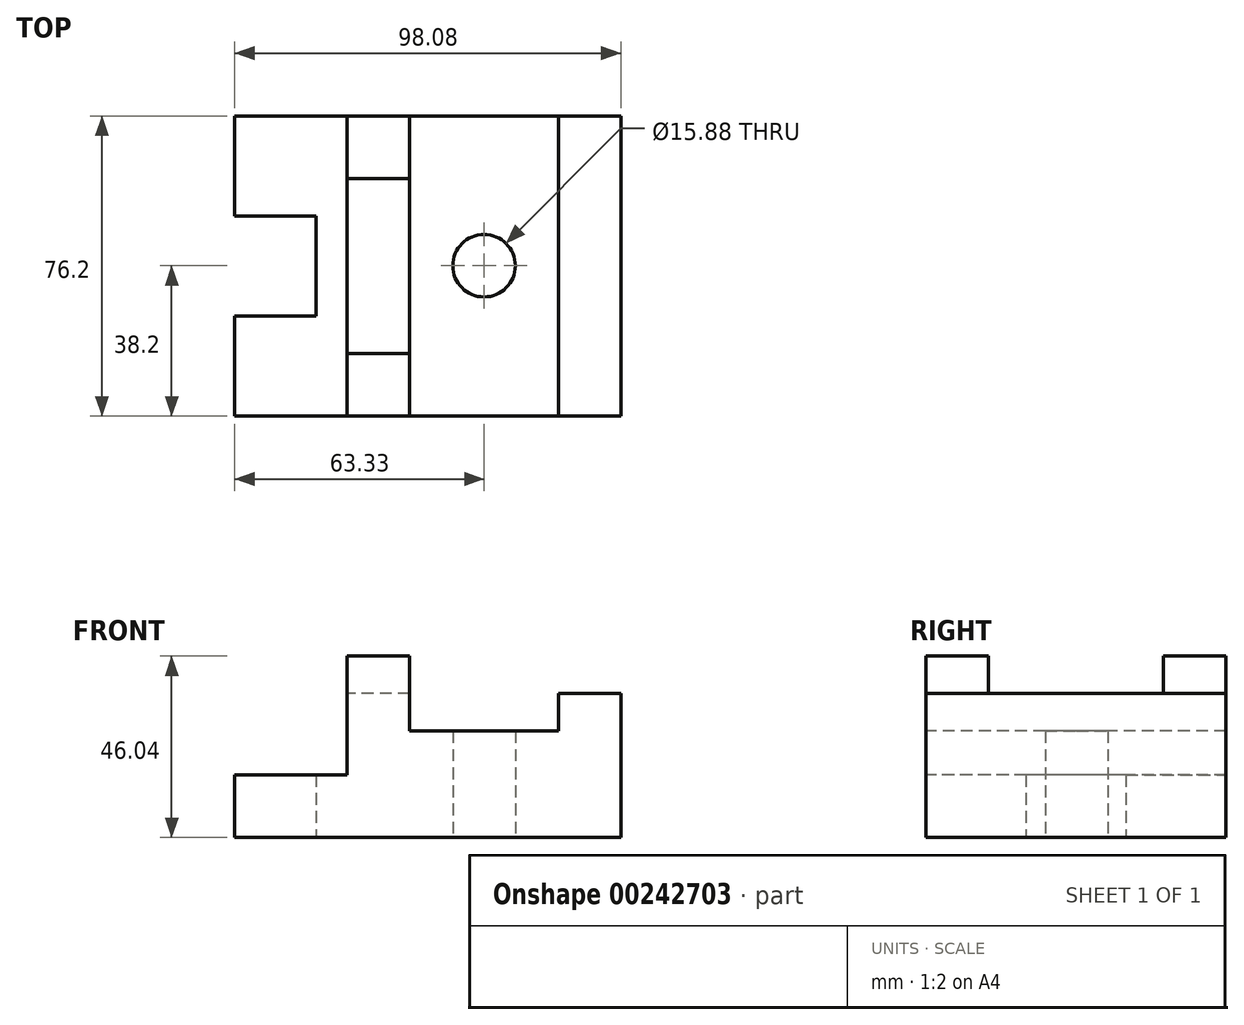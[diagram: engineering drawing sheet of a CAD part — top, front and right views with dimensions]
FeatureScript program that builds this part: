
annotation { "Feature Type Name" : "Feature", "Feature Type Description" : "" }
export const myFeature = defineFeature(function(context is Context, id is Id, definition is map)
    precondition{}
    {
        {
            var Q0;
            Q0=qCreatedBy(makeId("Top.planeOp"),FACE);
            var sketch = newSketch(context, id + "F0", { "sketchPlane" : qUnion([Q0])});
            skLineSegment(sketch, "E0.bottom", {"start": v(-127.34, 76) * mm, "end": v(126.66, 76) * mm});
            skLineSegment(sketch, "E0.top", {"start": v(-127.34, -76.4) * mm, "end": v(126.66, -76.4) * mm});
            skLineSegment(sketch, "E0.right", {"start": v(126.66, 76) * mm, "end": v(126.66, 25.2) * mm});
            skLineSegment(sketch, "E1", {"start": v(126.66, -76.4) * mm, "end": v(126.66, -25.6) * mm});
            skLineSegment(sketch, "E2", {"start": v(126.66, 25.2) * mm, "end": v(126.66, 76) * mm});
            skLineSegment(sketch, "E3", {"start": v(126.66, 25.2) * mm, "end": v(85.38, 25.2) * mm});
            skLineSegment(sketch, "E4", {"start": v(126.66, -25.6) * mm, "end": v(85.38, -25.6) * mm});
            skLineSegment(sketch, "E5", {"start": v(85.38, 25.2) * mm, "end": v(85.38, -25.6) * mm});
            skLineSegment(sketch, "E6", {"start": v(126.66, -76.4) * mm, "end": v(69.5, -76.4) * mm});
            skLineSegment(sketch, "E7", {"start": v(126.66, 76) * mm, "end": v(69.5, 76) * mm});
            skLineSegment(sketch, "E8", {"start": v(69.5, 76) * mm, "end": v(69.5, -76.4) * mm});
            skLineSegment(sketch, "E9", {"start": v(69.5, -76.4) * mm, "end": v(37.76, -76.4) * mm});
            skLineSegment(sketch, "E10", {"start": v(69.5, 76) * mm, "end": v(37.76, 76) * mm});
            skLineSegment(sketch, "E11", {"start": v(37.76, 76) * mm, "end": v(37.76, -76.4) * mm});
            skLineSegment(sketch, "E12", {"start": v(0, 76) * mm, "end": v(0, -76.4) * mm});
            skPoint(sketch, "E12.startSnap0", {"position": v(-0.34, 76) * mm});
            skLineSegment(sketch, "E13", {"start": v(37.76, 76) * mm, "end": v(37.76, 44.25) * mm});
            skLineSegment(sketch, "E14", {"start": v(37.76, 44.25) * mm, "end": v(69.5, 44.25) * mm});
            skLineSegment(sketch, "E15", {"start": v(69.5, 44.25) * mm, "end": v(69.5, 76) * mm});
            skLineSegment(sketch, "E16", {"start": v(37.76, -76.4) * mm, "end": v(37.76, -44.65) * mm});
            skLineSegment(sketch, "E17", {"start": v(37.76, -44.65) * mm, "end": v(69.5, -44.65) * mm});
            skLineSegment(sketch, "E18", {"start": v(69.5, -44.65) * mm, "end": v(69.5, -76.4) * mm});
            skCircle(sketch, "E19", {"center": v(0, 0) * mm, "radius": 15.88 * mm});
            skLineSegment(sketch, "E20.trimOffspring", {"start": v(126.66, -25.6) * mm, "end": v(126.66, -76.4) * mm});
            skLineSegment(sketch, "E21.MirrorCS", {"start": v(-37.76, 76) * mm, "end": v(-37.76, 44.25) * mm});
            skLineSegment(sketch, "E22.MirrorCS", {"start": v(-37.76, 76) * mm, "end": v(-37.76, -76.4) * mm});
            skLineSegment(sketch, "E23.MirrorCS", {"start": v(-37.76, -44.65) * mm, "end": v(-69.5, -44.65) * mm});
            skLineSegment(sketch, "E24.MirrorCS", {"start": v(-69.5, 76) * mm, "end": v(-69.5, -76.4) * mm});
            skLineSegment(sketch, "E25.MirrorCS", {"start": v(-69.5, -76.4) * mm, "end": v(-37.76, -76.4) * mm});
            skLineSegment(sketch, "E26.MirrorCS", {"start": v(-126.66, -25.6) * mm, "end": v(-85.38, -25.6) * mm});
            skLineSegment(sketch, "E27.MirrorCS", {"start": v(-126.66, -25.6) * mm, "end": v(-126.66, -76.4) * mm});
            skLineSegment(sketch, "E28.MirrorCS", {"start": v(-85.38, 25.2) * mm, "end": v(-85.38, -25.6) * mm});
            skLineSegment(sketch, "E29.MirrorCS", {"start": v(-126.66, 25.2) * mm, "end": v(-85.38, 25.2) * mm});
            skLineSegment(sketch, "E30.MirrorCS", {"start": v(-126.66, 25.2) * mm, "end": v(-126.66, 76) * mm});
            skLineSegment(sketch, "E31.MirrorCS", {"start": v(-126.66, 76) * mm, "end": v(-69.5, 76) * mm});
            skLineSegment(sketch, "E32.MirrorCS", {"start": v(-37.76, 44.25) * mm, "end": v(-69.5, 44.25) * mm});
            skPoint(sketch, "E33.MirrorCS.end.orphan", {"position": v(-69.5, -76.4) * mm});
            skPoint(sketch, "E33.MirrorCS.start.orphan", {"position": v(-126.66, -76.4) * mm});
            skLineSegment(sketch, "E34", {"start": v(-126.66, 76) * mm, "end": v(-126.66, 25.2) * mm});
            skSolve(sketch);
        }
        {
            var Q0;
            Q0=makeQuery(id+"F0.imprint","IMPRINT",FACE,{"disambiguationData":[TD([[makeQuery(id+"F0.imprint","IMPRINT",EDGE,{"derivedFrom":sQuery(id+"F0.wireOp",EDGE,"E2")}),1.0]])]});
            var Q1;
            Q1=makeQuery(id+"F0.imprint","IMPRINT",FACE,{"disambiguationData":[TD([[makeQuery(id+"F0.imprint","IMPRINT",EDGE,{"derivedFrom":sQuery(id+"F0.wireOp",EDGE,"E26.MirrorCS")}),-1.0]])]});
            extrude(context, id + "F1", {"entities" : qUnion([Q0, Q1]), "depth" : 31.75 * mm});
        }
        {
            var Q0;
            Q0=makeQuery(id+"F0.imprint","IMPRINT",FACE,{"disambiguationData":[TD([[makeQuery(id+"F0.imprint","IMPRINT",EDGE,{"derivedFrom":sQuery(id+"F0.wireOp",EDGE,"E10")}),1.0]])]});
            var Q1;
            Q1=makeQuery(id+"F0.imprint","IMPRINT",FACE,{"disambiguationData":[TD([[makeQuery(id+"F0.imprint","IMPRINT",EDGE,{"derivedFrom":sQuery(id+"F0.wireOp",EDGE,"E9")}),-1.0]])]});
            var Q2;
            {var subQ5=sQuery(id+"F0.wireOp",EDGE,"E32.MirrorCS");Q2=makeQuery(id+"F0.imprint","IMPRINT",FACE,{"disambiguationData":[TD([[makeQuery(id+"F0.imprint","IMPRINT",EDGE,{"derivedFrom":subQ5}),-1.0]])]});}
            var Q3;
            {var subQ0=sQuery(id+"F0.wireOp",EDGE,"E23.MirrorCS");Q3=makeQuery(id+"F0.imprint","IMPRINT",FACE,{"disambiguationData":[TD([[makeQuery(id+"F0.imprint","IMPRINT",EDGE,{"derivedFrom":subQ0}),1.0]])]});}
            extrude(context, id + "F2", {"entities" : qUnion([Q0, Q1, Q2, Q3]), "operationType" : NewBodyOperationType.ADD, "depth" : 92.07 * mm});
        }
        {
            var Q0;
            Q0=makeQuery(id+"F0.imprint","IMPRINT",FACE,{"disambiguationData":[TD([[makeQuery(id+"F0.imprint","IMPRINT",EDGE,{"derivedFrom":sQuery(id+"F0.wireOp",EDGE,"E8")}),-1.0]])]});
            var Q1;
            {var subQ0=sQuery(id+"F0.wireOp",EDGE,"E23.MirrorCS");Q1=makeQuery(id+"F0.imprint","IMPRINT",FACE,{"disambiguationData":[TD([[makeQuery(id+"F0.imprint","IMPRINT",EDGE,{"derivedFrom":subQ0}),-1.0]])]});}
            extrude(context, id + "F3", {"entities" : qUnion([Q0, Q1]), "operationType" : NewBodyOperationType.ADD, "depth" : 73.02 * mm});
        }
        {
            var Q0;
            Q0=makeQuery(id+"F0.imprint","IMPRINT",FACE,{"disambiguationData":[TD([[makeQuery(id+"F0.imprint","IMPRINT",EDGE,{"derivedFrom":sQuery(id+"F0.wireOp",EDGE,"E11")}),-1.0]])]});
            var Q1;
            {var subQ0=sQuery(id+"F0.wireOp",EDGE,"E12");var subQ9=sQuery(id+"F0.wireOp",EDGE,"E0.bottom");var subQ10=makeQuery(id+"F0.imprint","INTERSECT",VERTEX,{"derivedFrom":[subQ9,subQ0]});Q1=makeQuery(id+"F0.imprint","IMPRINT",FACE,{"disambiguationData":[TD([[makeQuery(id+"F0.imprint","IMPRINT",EDGE,{"disambiguationData":[TD([[subQ10,1.0]])],"derivedFrom":subQ9}),-1.0]])]});}
            extrude(context, id + "F4", {"entities" : qUnion([Q0, Q1]), "operationType" : NewBodyOperationType.ADD, "depth" : 53.97 * mm});
        }
        {
            var Q0;
            Q0=makeQuery(id+"F1.opExtrude","SWEPT_BODY",BODY,{"disambiguationData":[OSD([sQuery(id+"F0.wireOp",EDGE,"E0.top"),sQuery(id+"F0.wireOp",EDGE,"E24.MirrorCS"),sQuery(id+"F0.wireOp",EDGE,"E26.MirrorCS"),sQuery(id+"F0.wireOp",EDGE,"E28.MirrorCS"),sQuery(id+"F0.wireOp",EDGE,"E29.MirrorCS"),sQuery(id+"F0.wireOp",EDGE,"E31.MirrorCS"),sQuery(id+"F0.wireOp",EDGE,"E34"),sQuery(id+"F0.wireOp",EDGE,"E27.MirrorCS")])]});
            var Q1;
            Q1=makeQuery(id+"F1.opExtrude","SWEPT_BODY",BODY,{"disambiguationData":[OSD([sQuery(id+"F0.wireOp",EDGE,"E2"),sQuery(id+"F0.wireOp",EDGE,"E3"),sQuery(id+"F0.wireOp",EDGE,"E4"),sQuery(id+"F0.wireOp",EDGE,"E5"),sQuery(id+"F0.wireOp",EDGE,"E6"),sQuery(id+"F0.wireOp",EDGE,"E7"),sQuery(id+"F0.wireOp",EDGE,"E8"),sQuery(id+"F0.wireOp",EDGE,"E15"),sQuery(id+"F0.wireOp",EDGE,"E18"),sQuery(id+"F0.wireOp",EDGE,"E20.trimOffspring")])]});
            var Q2;
            Q2=makeQuery(id+"F2.opExtrude","SWEPT_BODY",BODY,{"disambiguationData":[OSD([sQuery(id+"F0.wireOp",EDGE,"E0.bottom"),sQuery(id+"F0.wireOp",EDGE,"E24.MirrorCS"),sQuery(id+"F0.wireOp",EDGE,"E22.MirrorCS"),sQuery(id+"F0.wireOp",EDGE,"E32.MirrorCS")])]});
            var Q3;
            Q3=makeQuery(id+"F2.opExtrude","SWEPT_BODY",BODY,{"disambiguationData":[OSD([sQuery(id+"F0.wireOp",EDGE,"E23.MirrorCS"),sQuery(id+"F0.wireOp",EDGE,"E24.MirrorCS"),sQuery(id+"F0.wireOp",EDGE,"E25.MirrorCS"),sQuery(id+"F0.wireOp",EDGE,"E22.MirrorCS")])]});
            var Q4;
            Q4=makeQuery(id+"F3.opExtrude","SWEPT_BODY",BODY,{"disambiguationData":[OSD([sQuery(id+"F0.wireOp",EDGE,"E23.MirrorCS"),sQuery(id+"F0.wireOp",EDGE,"E24.MirrorCS"),sQuery(id+"F0.wireOp",EDGE,"E22.MirrorCS"),sQuery(id+"F0.wireOp",EDGE,"E32.MirrorCS")])]});
            var Q5;
            Q5=qCreatedBy(makeId("Origin.pointOp"),VERTEX);
            transform(context, id + "F5", {"entities" : qUnion([Q0, Q1, Q2, Q3, Q4]), "transformType" : TransformType.SCALE_UNIFORMLY, "scale" : .5, "scalePoint" : qUnion([Q5]), "makeCopy" : false});
        }
    });
